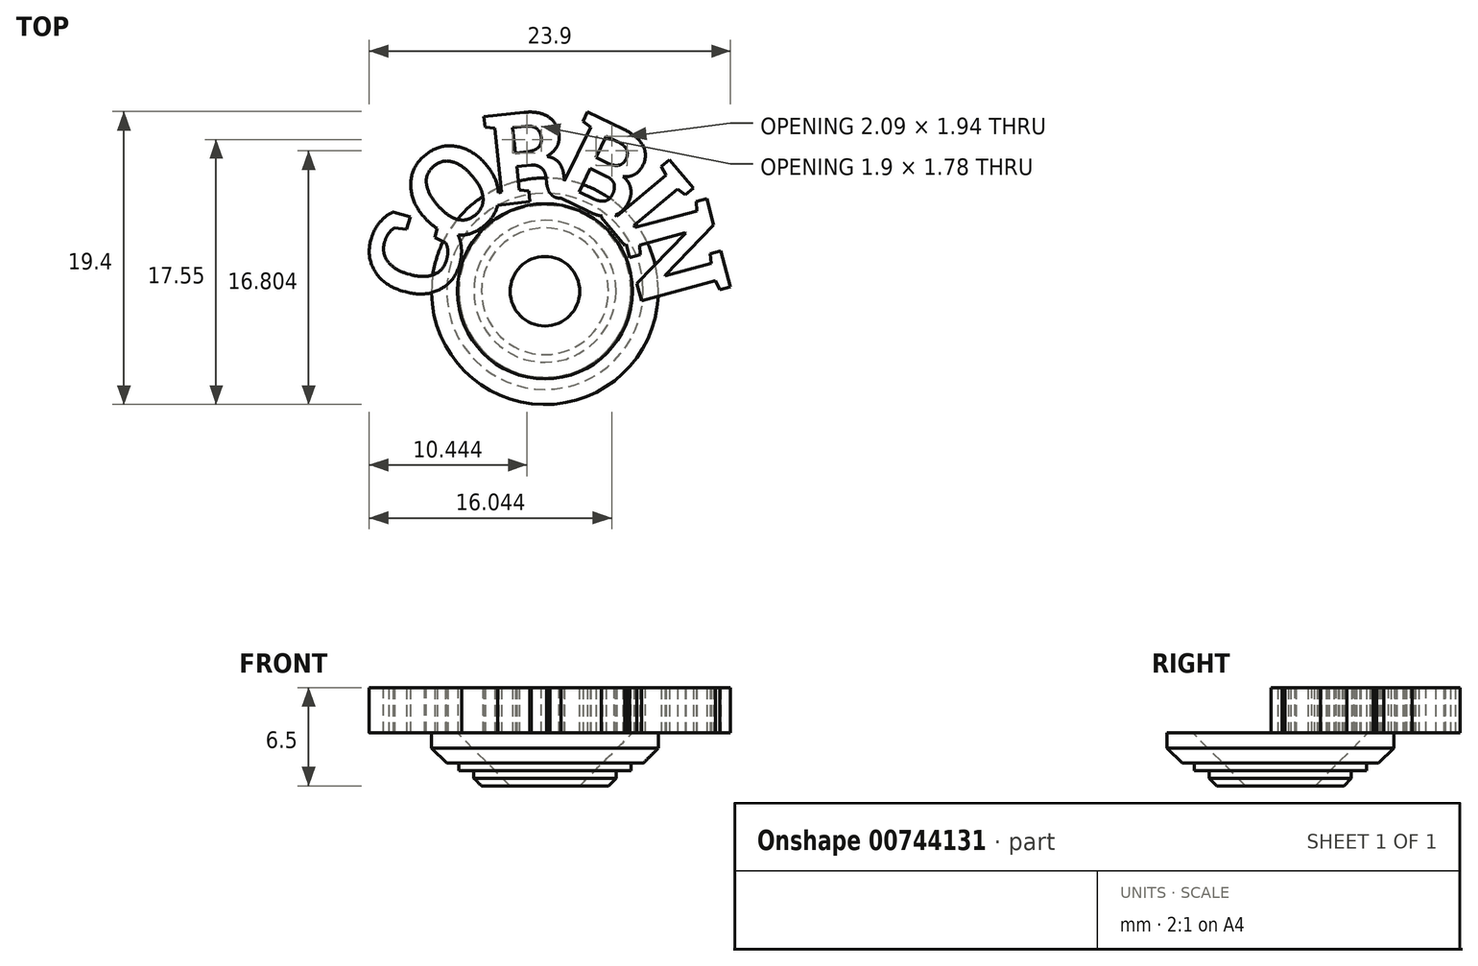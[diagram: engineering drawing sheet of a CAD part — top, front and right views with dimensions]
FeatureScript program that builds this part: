
annotation { "Feature Type Name" : "Feature", "Feature Type Description" : "" }
export const myFeature = defineFeature(function(context is Context, id is Id, definition is map)
    precondition{}
    {
        {
            var Q0;
            Q0=qCreatedBy(makeId("Top.planeOp"),FACE);
            var sketch = newSketch(context, id + "F0", { "sketchPlane" : qUnion([Q0])});
            skCircle(sketch, "E0", {"center": v(0, 0) * mm, "radius": 7.5 * mm});
            skLineSegment(sketch, "E1", {"start": v(0, 19.33) * mm, "end": v(0, -22.56) * mm, "construction": true});
            skLineSegment(sketch, "E2", {"start": v(17.52, 0) * mm, "end": v(-21.05, 0) * mm, "construction": true});
            skSolve(sketch);
        }
        {
            var Q0;
            Q0=qSketchRegion(id+"F0",true);
            extrude(context, id + "F1", {"entities" : qUnion([Q0]), "depth" : 2 * mm, "offsetDistance" : 25 * mm});
        }
        {
            var Q0;
            Q0=makeQuery(id+"F1.opExtrude","CAP_FACE",FACE,{"disambiguationData":[OSD([sQuery(id+"F0.wireOp",EDGE,"E0")])],"isStart":true});
            var sketch = newSketch(context, id + "F2", { "sketchPlane" : qUnion([Q0])});
            skCircle(sketch, "E3", {"center": v(0, 0) * mm, "radius": 4.7 * mm});
            skSolve(sketch);
        }
        {
            var Q0;
            Q0=qSketchRegion(id+"F2",true);
            extrude(context, id + "F3", {"entities" : qUnion([Q0]), "operationType" : NewBodyOperationType.ADD, "depth" : 1.5 * mm, "offsetDistance" : 25 * mm});
        }
        {
            var Q0;
            Q0=makeQuery(id+"F3.opExtrude","CAP_EDGE",EDGE,{"disambiguationData":[OSD([sQuery(id+"F2.wireOp",EDGE,"E3")])],"isStart":false});
            chamfer(context, id + "F4", {"entities" : qUnion([Q0]), "width" : .5 * mm, "tangentPropagation" : true});
        }
        {
            var Q0;
            Q0=makeQuery(id+"F3.opExtrude","CAP_FACE",FACE,{"disambiguationData":[OSD([sQuery(id+"F2.wireOp",EDGE,"E3")])],"isStart":false});
            var sketch = newSketch(context, id + "F5", { "sketchPlane" : qUnion([Q0])});
            skCircle(sketch, "E4", {"center": v(0, 0) * mm, "radius": 1.5 * mm});
            skSolve(sketch);
        }
        {
            var Q0;
            Q0=qSketchRegion(id+"F5",true);
            extrude(context, id + "F6", {"entities" : qUnion([Q0]), "operationType" : NewBodyOperationType.REMOVE, "oppositeDirection" : true, "depth" : 25 * mm, "offsetDistance" : 25 * mm});
        }
        {
            var Q0;
            Q0=makeQuery(id+"F1.opExtrude","CAP_FACE",FACE,{"disambiguationData":[OSD([sQuery(id+"F0.wireOp",EDGE,"E0")])],"isStart":true});
            var sketch = newSketch(context, id + "F7", { "sketchPlane" : qUnion([Q0])});
            skCircle(sketch, "E5.0", {"center": v(0, 0) * mm, "radius": 5.7 * mm});
            skCircle(sketch, "E6.0", {"center": v(0, 0) * mm, "radius": 4.7 * mm});
            skSolve(sketch);
        }
        {
            var Q0;
            Q0=qSketchRegion(id+"F7",true);
            extrude(context, id + "F8", {"entities" : qUnion([Q0]), "operationType" : NewBodyOperationType.ADD, "depth" : .5 * mm, "offsetDistance" : 25 * mm});
        }
        {
            var Q0;
            Q0=makeQuery(id+"F1.opExtrude","CAP_FACE",FACE,{"disambiguationData":[OSD([sQuery(id+"F0.wireOp",EDGE,"E0")])],"isStart":false});
            var sketch = newSketch(context, id + "F9", { "sketchPlane" : qUnion([Q0])});
            skText(sketch, "E7", { "text": "C", "fontName": "RobotoSlab-Bold.ttf"});
            skText(sketch, "E8", { "text": "O", "fontName": "RobotoSlab-Bold.ttf"});
            skText(sketch, "E9", { "text": "B", "fontName": "RobotoSlab-Bold.ttf"});
            skText(sketch, "E10", { "text": "R", "fontName": "RobotoSlab-Bold.ttf"});
            skLineSegment(sketch, "E11", {"start": v(0, 0) * mm, "end": v(-14.65, 4.2) * mm, "construction": true});
            skLineSegment(sketch, "E12", {"start": v(0, 0) * mm, "end": v(6.95, 14.26) * mm, "construction": true});
            skLineSegment(sketch, "E13", {"start": v(0, 0) * mm, "end": v(-1.78, 16.95) * mm, "construction": true});
            skLineSegment(sketch, "E14", {"start": v(0, 0) * mm, "end": v(-10.5, 12.08) * mm, "construction": true});
            skLineSegment(sketch, "E15", {"start": v(0, 0) * mm, "end": v(21.4, 0) * mm, "construction": true});
            skLineSegment(sketch, "E16", {"start": v(0, 0) * mm, "end": v(16.04, 13.46) * mm, "construction": true});
            skLineSegment(sketch, "E17", {"start": v(0, 0) * mm, "end": v(20.52, 5.5) * mm, "construction": true});
            skText(sketch, "E18", { "text": "I", "fontName": "RobotoSlab-Bold.ttf"});
            skText(sketch, "E19", { "text": "N", "fontName": "RobotoSlab-Bold.ttf"});
            const initialGuessF9  = {"E7": [-0.00654, -0.00103, 0.27564, 0.96126, 0.006], "E8": [-0.00626, 0.0025, 0.7547, 0.65606, 0.006], "E9": [2e-05, 0.00667, 0.8988, -0.43837, 0.006], "E10": [-0.00365, 0.00565, 0.99452, 0.10453, 0.006], "E18": [0.00357, 0.00508, 0.64279, -0.76604, 0.006], "E19": [0.00492, 0.00483, 0.25882, -0.96593, 0.006]};
            skSetInitialGuess(sketch, initialGuessF9);
            skSolve(sketch);
        }
        {
            var Q0;
            Q0=qSketchRegion(id+"F9",true);
            extrude(context, id + "F10", {"entities" : qUnion([Q0]), "operationType" : NewBodyOperationType.ADD, "depth" : 3 * mm, "offsetDistance" : 25 * mm});
        }
        {
            var Q0;
            Q0=makeQuery(id+"F6.boolean.opBoolean","INTERSECT",EDGE,{"derivedFrom":[makeQuery(id+"F1.opExtrude","CAP_FACE",FACE,{"disambiguationData":[OSD([sQuery(id+"F0.wireOp",EDGE,"E0")])],"isStart":false}),makeQuery(id+"F6.opExtrude","SWEPT_FACE",FACE,{"disambiguationData":[OSD([sQuery(id+"F5.wireOp",EDGE,"E4")])]})]});
            chamfer(context, id + "F11", {"entities" : qUnion([Q0]), "width" : 4.3 * mm, "tangentPropagation" : true});
        }
        {
            var Q0;
            Q0=makeQuery(id+"F1.opExtrude","CAP_EDGE",EDGE,{"disambiguationData":[OSD([sQuery(id+"F0.wireOp",EDGE,"E0")])],"isStart":true});
            chamfer(context, id + "F12", {"entities" : qUnion([Q0]), "width" : 1 * mm, "tangentPropagation" : true});
        }
    });
